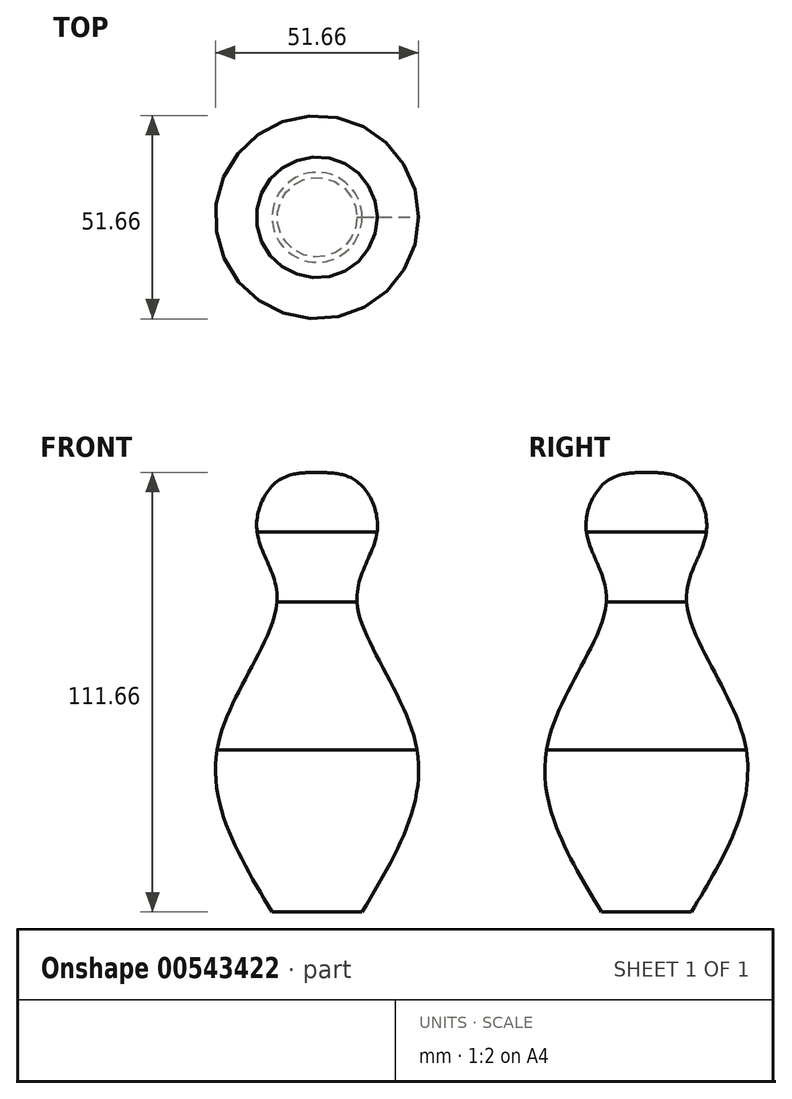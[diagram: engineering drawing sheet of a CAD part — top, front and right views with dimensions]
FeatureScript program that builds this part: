
annotation { "Feature Type Name" : "Feature", "Feature Type Description" : "" }
export const myFeature = defineFeature(function(context is Context, id is Id, definition is map)
    precondition{}
    {
        {
            var Q0;
            Q0=qCreatedBy(makeId("Front.planeOp"),FACE);
            var sketch = newSketch(context, id + "F0", { "sketchPlane" : qUnion([Q0])});
            skLineSegment(sketch, "E0", {"start": v(0, 57.61) * mm, "end": v(0, -56.69) * mm});
            skLineSegment(sketch, "E1", {"start": v(0, 39.83) * mm, "end": v(15.24, 39.83) * mm});
            skLineSegment(sketch, "E2", {"start": v(0, 22.05) * mm, "end": v(10.16, 22.05) * mm});
            skLineSegment(sketch, "E3", {"start": v(0, -15.51) * mm, "end": v(25.4, -15.51) * mm});
            skLineSegment(sketch, "E4", {"start": v(0, -56.69) * mm, "end": v(11.43, -56.69) * mm});
            skLineSegment(sketch, "E5", {"start": v(0, 52.66) * mm, "end": v(10.16, 52.66) * mm});
            skFitSpline(sketch, "E6", {"points": [v(11.43, -56.69) * mm, v(25.4, -15.51) * mm, v(10.16, 22.05) * mm, v(15.24, 39.83) * mm, v(10.16, 52.66) * mm, v(0, 54.97) * mm], "startDerivative": vector(90.21, 149.67) * mm, "endDerivative": vector(-81.6, 1.33) * mm});
            skSolve(sketch);
        }
        {
            var Q0;
            Q0 = qSketchRegion(id + "F0", true);
            var Q1;
            Q1=sQuery(id+"F0.wireOp",EDGE,"E0");
            revolve(context, id + "F1", {"surfaceOperationType" : NewSurfaceOperationType.NEW, "entities" : qUnion([Q0]), "axis" : qUnion([Q1]), "revolveType" : RevolveType.FULL});
        }
    });
